FCSTD DOCUMENT  (FreeCAD 1.0R39319 (Git))
Label: pipe
License: All rights reserved
LicenseURL: https://en.wikipedia.org/wiki/All_rights_reserved
objects: Sketcher::SketchObject×1, PartDesign::Body×1
note: 3 computed .brp shape members not serialized (recipe doc carries the construction recipe); baked Part::Feature solids carry a one-line shape summary decoded from their .brp

FEATURE [Sketcher::SketchObject] Sketch
  ArcFitTolerance = 1e-06
  AttachmentSupport = -> [XY_Plane]
  FullyConstrained = false
  MakeInternals = false
  MapMode = 5
  sketch-geometry (4):
    g0: LineSegment StartX=-15.8977 StartY=-5.77394 StartZ=0 EndX=-15.8977 EndY=-19.4739 EndZ=0
    g1: LineSegment StartX=-15.8977 StartY=-19.4739 StartZ=0 EndX=16.0023 EndY=-19.4739 EndZ=0
    g2: LineSegment StartX=16.0023 StartY=-19.4739 StartZ=0 EndX=16.0023 EndY=-5.77394 EndZ=0
    g3: LineSegment StartX=16.0023 StartY=-5.77394 StartZ=0 EndX=-15.8977 EndY=-5.77394 EndZ=0
  constraints (10):
    c: Coincident(g0,g1)
    c: Coincident(g1,g2)
    c: Coincident(g2,g3)
    c: Coincident(g3,g0)
    c: Vertical(g0)
    c: Vertical(g2)
    c: Horizontal(g1)
    c: Horizontal(g3)
    c: Distance(g0,g2) = 31.9
    c: Distance(g1,g3) = 13.7
FEATURE [PartDesign::Body] Body
  AllowCompound = false
  Group = -> [Sketch]
  Origin = -> Origin
